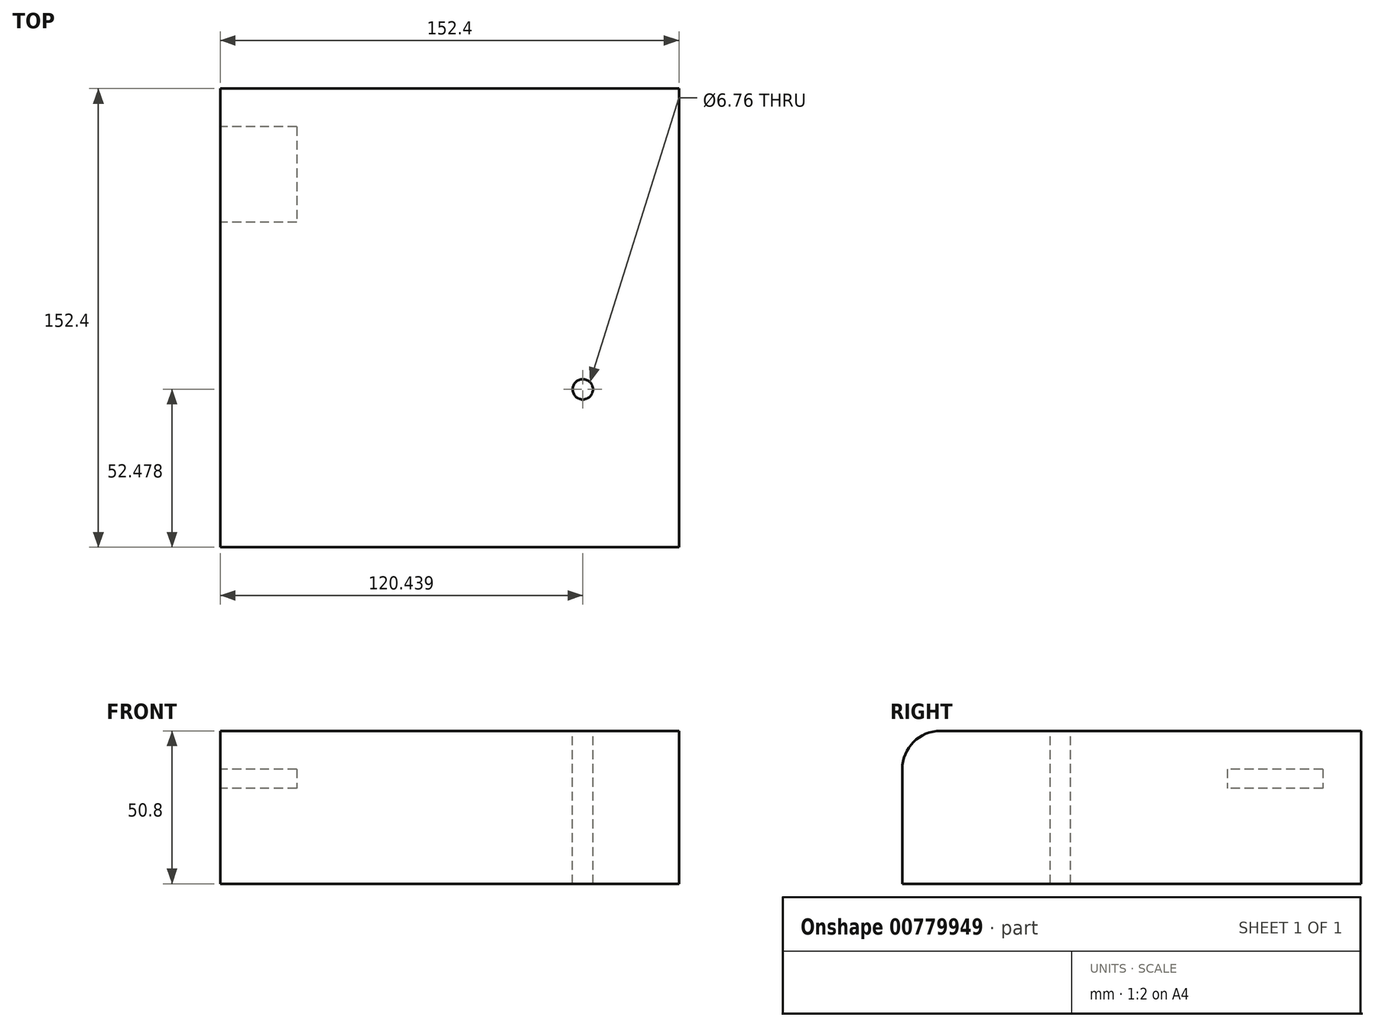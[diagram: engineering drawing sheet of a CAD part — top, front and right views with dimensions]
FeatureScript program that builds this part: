
annotation { "Feature Type Name" : "Feature", "Feature Type Description" : "" }
export const myFeature = defineFeature(function(context is Context, id is Id, definition is map)
    precondition{}
    {
        {
            var Q0;
            Q0=qCreatedBy(makeId("Front.planeOp"),FACE);
            var sketch = newSketch(context, id + "F0", { "sketchPlane" : qUnion([Q0])});
            skLineSegment(sketch, "E0.bottom", {"start": v(-76.2, 25.4) * mm, "end": v(76.2, 25.4) * mm});
            skLineSegment(sketch, "E0.top", {"start": v(-76.2, -25.4) * mm, "end": v(76.2, -25.4) * mm});
            skLineSegment(sketch, "E0.left", {"start": v(-76.2, 25.4) * mm, "end": v(-76.2, -25.4) * mm});
            skLineSegment(sketch, "E0.right", {"start": v(76.2, 25.4) * mm, "end": v(76.2, -25.4) * mm});
            skLineSegment(sketch, "E1", {"start": v(-76.2, -25.4) * mm, "end": v(76.2, 25.4) * mm, "construction": true});
            skSolve(sketch);
        }
        {
            var Q0;
            Q0 = qSketchRegion(id + "F0", true);
            extrude(context, id + "F1", {"entities" : qUnion([Q0]), "endBound" : BoundingType.SYMMETRIC, "depth" : 152.4 * mm, "offsetDistance" : 25.4 * mm});
        }
        {
            var Q0;
            Q0=makeQuery(id+"F1.opExtrude","CAP_EDGE",EDGE,{"disambiguationData":[OSD([sQuery(id+"F0.wireOp",EDGE,"E0.bottom")])],"isStart":false});
            fillet(context, id + "F2", {"entities" : qUnion([Q0]), "radius" : 12.7 * mm, "tangentPropagation" : true, "allowEdgeOverflow" : false});
        }
        {
            var Q0;
            Q0=makeQuery(id+"F1.opExtrude","SWEPT_FACE",FACE,{"disambiguationData":[OSD([sQuery(id+"F0.wireOp",EDGE,"E0.bottom")])]});
            var sketch = newSketch(context, id + "F3", { "sketchPlane" : qUnion([Q0])});
            skPoint(sketch, "E2", {"position": v(44.24, -23.72) * mm});
            skSolve(sketch);
        }
        {
            var Q0;
            Q0=sQuery(id+"F3.wireOp",VERTEX,"E2");
            var Q1;
            Q1=makeQuery(id+"F1.opExtrude","SWEPT_BODY",BODY,{"disambiguationData":[OSD([sQuery(id+"F0.wireOp",EDGE,"E0.bottom"),sQuery(id+"F0.wireOp",EDGE,"E0.top"),sQuery(id+"F0.wireOp",EDGE,"E0.left"),sQuery(id+"F0.wireOp",EDGE,"E0.right")])]});
            hole(context, id + "F4", {"style" : HoleStyle.SIMPLE, "endStyle" : HoleEndStyle.THROUGH, "standardTappedOrClearance" : lookupTablePath({ "standard" : "ANSI", "fit" : "Normal (ASME)", "size" : "1/4", "type" : "Clearance" }), "standardBlindInLast" : lookupTablePath({ "fit" : "Free", "standard" : "ANSI", "size" : "1/4", "type" : "Clearance" }), "holeDiameter" : 6.76 * mm, "majorDiameter" : 6.35 * mm, "isTappedThrough" : true, "tappedDepth" : 12.7 * mm, "tapClearance" : 3, "locations" : qUnion([Q0]), "scope" : qUnion([Q1])});
        }
        {
            var Q0;
            Q0=makeQuery(id+"F1.opExtrude","SWEPT_FACE",FACE,{"disambiguationData":[OSD([sQuery(id+"F0.wireOp",EDGE,"E0.left")])]});
            var sketch = newSketch(context, id + "F5", { "sketchPlane" : qUnion([Q0])});
            skLineSegment(sketch, "E3.bottom", {"start": v(-63.5, 6.35) * mm, "end": v(-31.75, 6.35) * mm});
            skLineSegment(sketch, "E3.top", {"start": v(-63.5, 12.7) * mm, "end": v(-31.75, 12.7) * mm});
            skLineSegment(sketch, "E3.left", {"start": v(-63.5, 12.7) * mm, "end": v(-63.5, 6.35) * mm});
            skLineSegment(sketch, "E3.right", {"start": v(-31.75, 12.7) * mm, "end": v(-31.75, 6.35) * mm});
            skSolve(sketch);
        }
        {
            var Q0;
            Q0=makeQuery(id+"F5.imprint","IMPRINT",FACE,{"disambiguationData":[TD([[makeQuery(id+"F5.imprint","IMPRINT",EDGE,{"derivedFrom":sQuery(id+"F5.wireOp",EDGE,"E3.bottom")}),1.0]])]});
            extrude(context, id + "F6", {"entities" : qUnion([Q0]), "operationType" : NewBodyOperationType.REMOVE, "oppositeDirection" : true, "depth" : 25.4 * mm, "offsetDistance" : 25.4 * mm});
        }
    });
